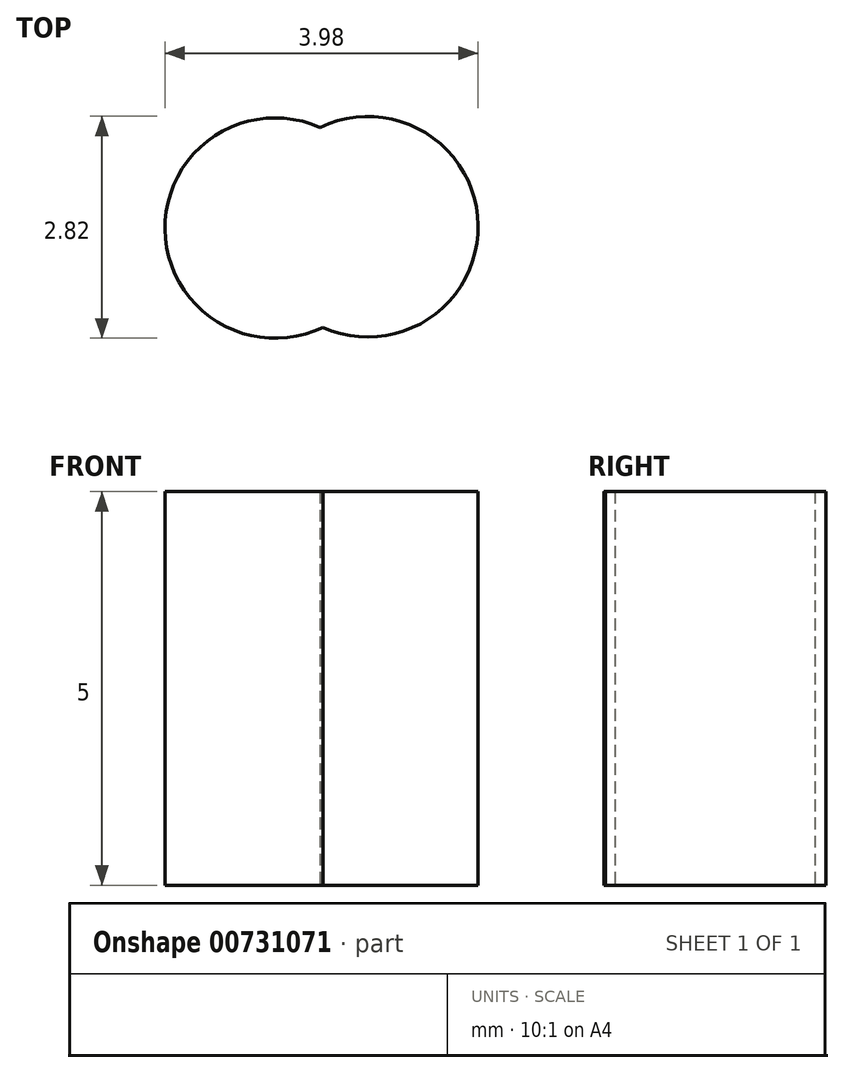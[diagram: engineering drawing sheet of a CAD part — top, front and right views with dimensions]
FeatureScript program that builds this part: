
annotation { "Feature Type Name" : "Feature", "Feature Type Description" : "" }
export const myFeature = defineFeature(function(context is Context, id is Id, definition is map)
    precondition{}
    {
        {
            var Q0;
            Q0=qCreatedBy(makeId("Top.planeOp"),FACE);
            var sketch = newSketch(context, id + "F0", { "sketchPlane" : qUnion([Q0])});
            skCircle(sketch, "E0", {"center": v(-771.54, 278.39) * mm, "radius": 1.4 * mm});
            skCircle(sketch, "E1", {"center": v(-772.72, 278.37) * mm, "radius": 1.4 * mm});
            skCircle(sketch, "E2", {"center": v(-772.13, 278.38) * mm, "radius": 2 * mm});
            skSolve(sketch);
        }
        {
            var Q0;
            {var subQ0=sQuery(id+"F0.wireOp",EDGE,"E1");var subQ1=sQuery(id+"F0.wireOp",EDGE,"E0");var subQ2=makeQuery(id+"F0.imprint","INTERSECT",VERTEX,{"disambiguationData":[OD(0.0)],"derivedFrom":[subQ1,subQ0]});Q0=makeQuery(id+"F0.imprint","IMPRINT",FACE,{"disambiguationData":[TD([[makeQuery(id+"F0.imprint","IMPRINT",EDGE,{"disambiguationData":[TD([[subQ2,1.0]])],"derivedFrom":subQ1}),-1.0]])]});}
            var Q1;
            {var subQ0=sQuery(id+"F0.wireOp",EDGE,"E1");var subQ1=sQuery(id+"F0.wireOp",EDGE,"E0");var subQ2=makeQuery(id+"F0.imprint","INTERSECT",VERTEX,{"disambiguationData":[OD(0.0)],"derivedFrom":[subQ1,subQ0]});Q1=makeQuery(id+"F0.imprint","IMPRINT",FACE,{"disambiguationData":[TD([[makeQuery(id+"F0.imprint","IMPRINT",EDGE,{"disambiguationData":[TD([[subQ2,1.0]])],"derivedFrom":subQ1}),1.0]])]});}
            var Q2;
            {var subQ0=sQuery(id+"F0.wireOp",EDGE,"E1");var subQ1=sQuery(id+"F0.wireOp",EDGE,"E0");var subQ2=makeQuery(id+"F0.imprint","INTERSECT",VERTEX,{"disambiguationData":[OD(0.0)],"derivedFrom":[subQ1,subQ0]});Q2=makeQuery(id+"F0.imprint","IMPRINT",FACE,{"disambiguationData":[TD([[makeQuery(id+"F0.imprint","IMPRINT",EDGE,{"disambiguationData":[TD([[subQ2,-1.0]])],"derivedFrom":subQ1}),1.0]])]});}
            extrude(context, id + "F1", {"entities" : qUnion([Q0, Q1, Q2]), "depth" : 5 * mm, "offsetDistance" : 25.4 * mm});
        }
    });
